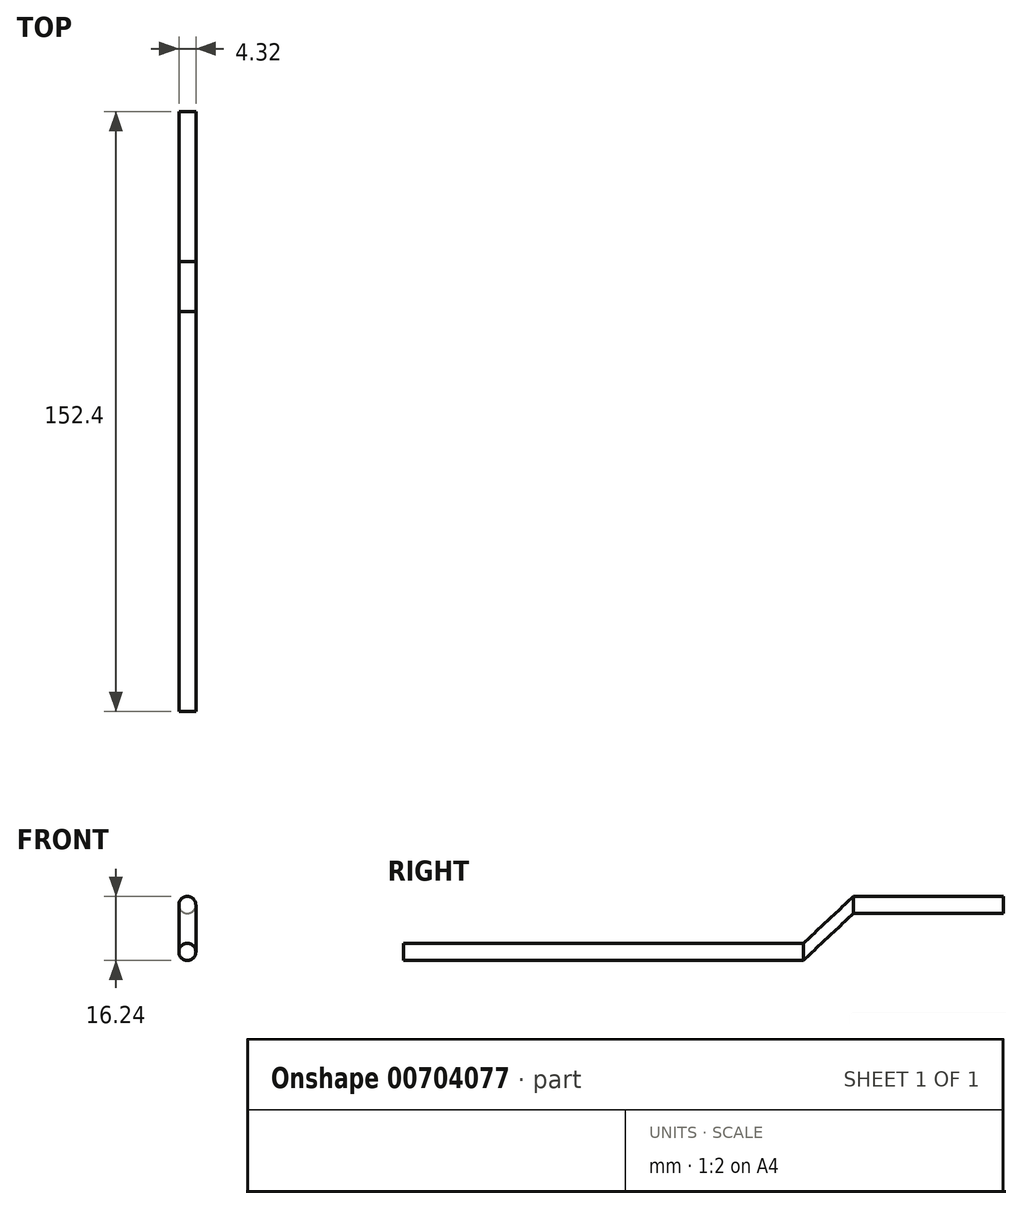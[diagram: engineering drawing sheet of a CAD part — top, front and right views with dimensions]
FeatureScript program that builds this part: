
annotation { "Feature Type Name" : "Feature", "Feature Type Description" : "" }
export const myFeature = defineFeature(function(context is Context, id is Id, definition is map)
    precondition{}
    {
        {
            var Q0;
            Q0=qCreatedBy(makeId("Front.planeOp"),FACE);
            var sketch = newSketch(context, id + "F0", { "sketchPlane" : qUnion([Q0])});
            skCircle(sketch, "E0", {"center": v(0, 0) * mm, "radius": 2.16 * mm});
            skSolve(sketch);
        }
        {
            var Q0;
            Q0 = qSketchRegion(id + "F0", true);
            extrude(context, id + "F1", {"entities" : qUnion([Q0]), "depth" : 101.6 * mm, "offsetDistance" : 25.4 * mm});
        }
        {
            var Q0;
            Q0=qCreatedBy(makeId("Front.planeOp"),FACE);
            var sketch = newSketch(context, id + "F2", { "sketchPlane" : qUnion([Q0])});
            skCircle(sketch, "E1", {"center": v(0, 11.92) * mm, "radius": 2.16 * mm});
            skSolve(sketch);
        }
        {
            var Q0;
            Q0=makeQuery(id+"F2.imprint","IMPRINT",FACE,{"disambiguationData":[TD([[makeQuery(id+"F2.imprint","IMPRINT",EDGE,{"derivedFrom":sQuery(id+"F2.wireOp",EDGE,"E1")}),1.0]])]});
            extrude(context, id + "F3", {"entities" : qUnion([Q0]), "oppositeDirection" : true, "depth" : 50.8 * mm, "offsetDistance" : 25.4 * mm, "hasSecondDirection" : true, "secondDirectionOppositeDirection" : true, "secondDirectionDepth" : 12.7 * mm});
        }
        {
            var Q0;
            Q0=makeQuery(id+"F1.opExtrude","CAP_FACE",FACE,{"disambiguationData":[OSD([sQuery(id+"F0.wireOp",EDGE,"E0")])],"isStart":true});
            var Q1;
            Q1=makeQuery(id+"F3.opExtrude","CAP_FACE",FACE,{"disambiguationData":[OSD([sQuery(id+"F2.wireOp",EDGE,"E1")])],"isStart":true});
            loft(context, id + "F4", {"sheetProfilesArray" : [{ "sheetProfileEntities" : qUnion([Q0]) }, { "sheetProfileEntities" : qUnion([Q1]) }]});
        }
    });
